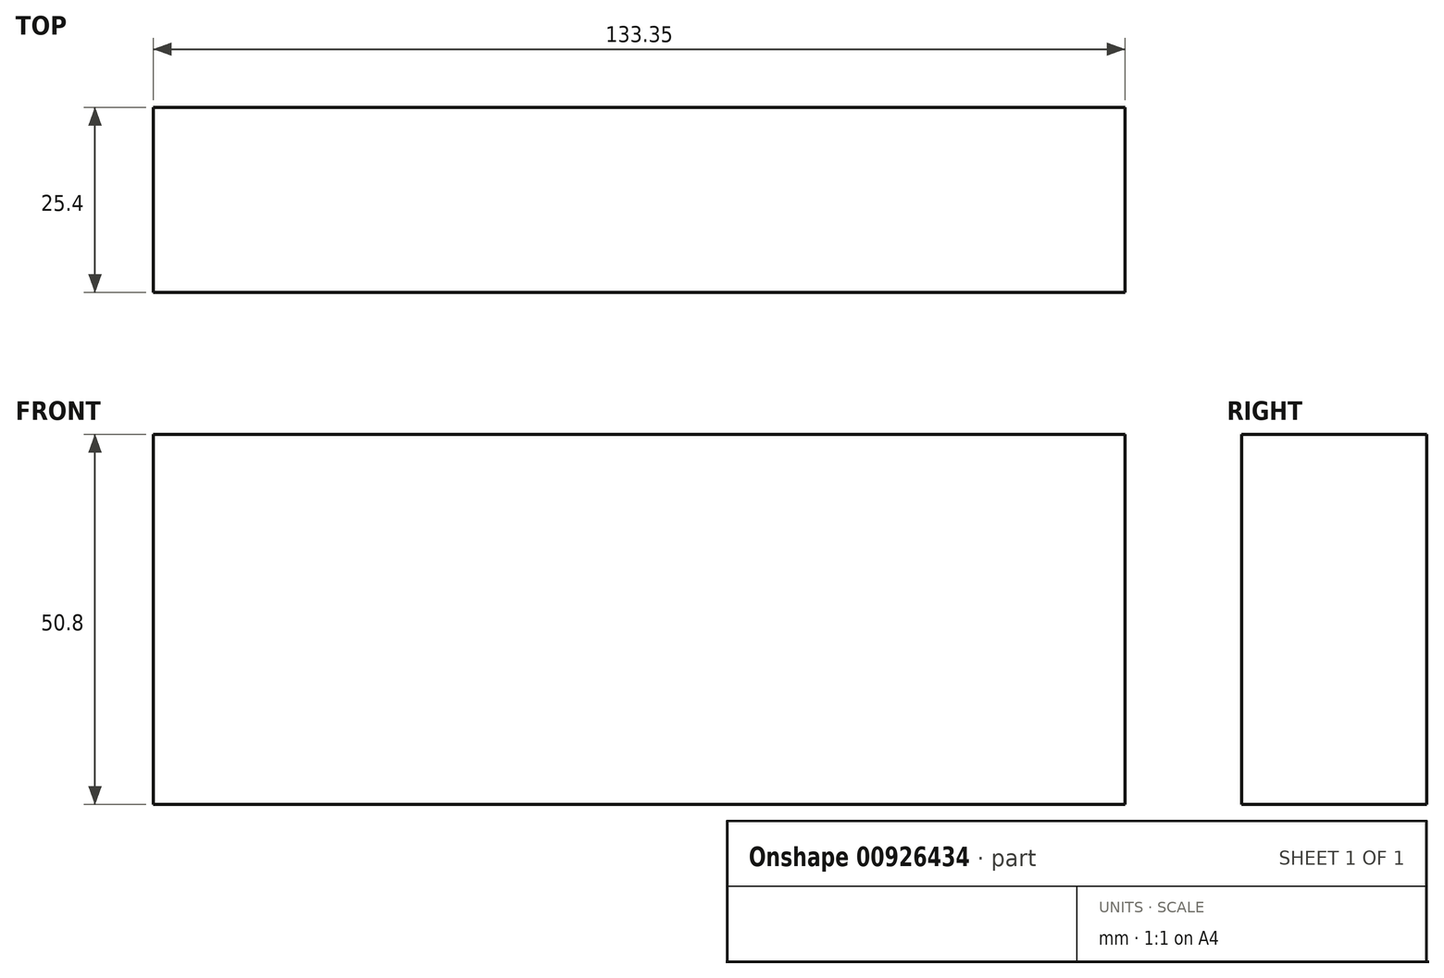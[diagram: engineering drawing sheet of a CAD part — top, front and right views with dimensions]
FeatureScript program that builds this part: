
annotation { "Feature Type Name" : "Feature", "Feature Type Description" : "" }
export const myFeature = defineFeature(function(context is Context, id is Id, definition is map)
    precondition{}
    {
        {
            var Q0;
            Q0=qCreatedBy(makeId("Front.planeOp"),FACE);
            var sketch = newSketch(context, id + "F0", { "sketchPlane" : qUnion([Q0])});
            skLineSegment(sketch, "E0", {"start": v(-76.87, -33.84) * mm, "end": v(56.48, -33.84) * mm});
            skLineSegment(sketch, "E1", {"start": v(56.48, -33.84) * mm, "end": v(56.48, 16.96) * mm});
            skLineSegment(sketch, "E2", {"start": v(56.48, 16.96) * mm, "end": v(-76.87, 16.96) * mm});
            skLineSegment(sketch, "E3", {"start": v(-76.87, 16.96) * mm, "end": v(-76.87, -33.84) * mm});
            skSolve(sketch);
        }
        {
            var Q0;
            Q0 = qSketchRegion(id + "F0", true);
            extrude(context, id + "F1", {"entities" : qUnion([Q0]), "depth" : 25.4 * mm, "offsetDistance" : 25.4 * mm});
        }
    });
